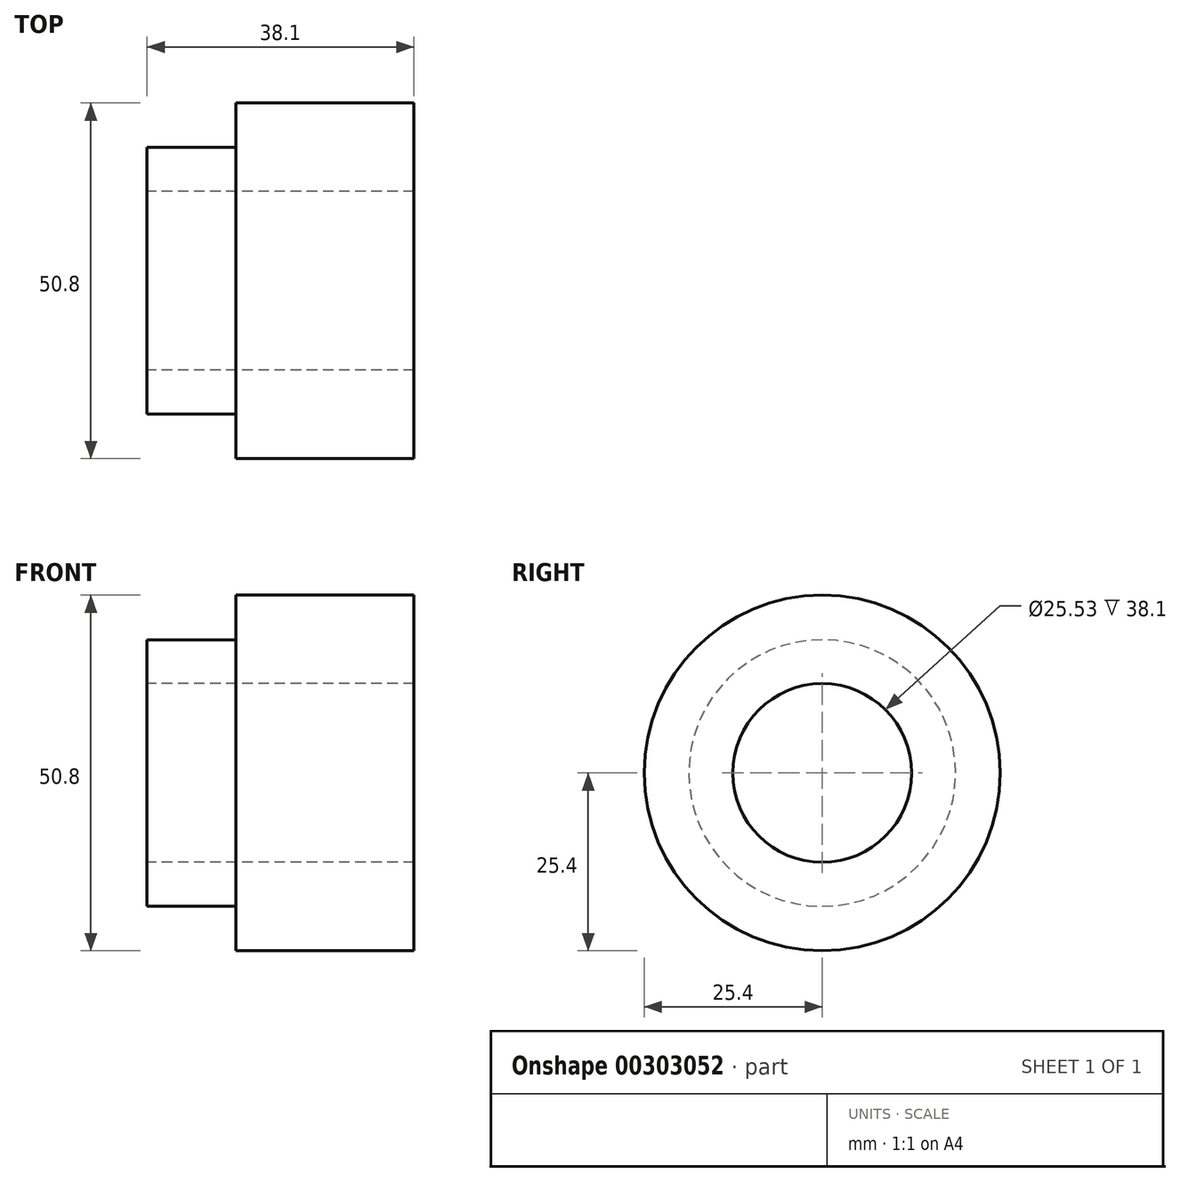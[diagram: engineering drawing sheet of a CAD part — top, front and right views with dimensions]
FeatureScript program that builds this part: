
annotation { "Feature Type Name" : "Feature", "Feature Type Description" : "" }
export const myFeature = defineFeature(function(context is Context, id is Id, definition is map)
    precondition{}
    {
        {
            var Q0;
            Q0=qCreatedBy(makeId("Front.planeOp"),FACE);
            var sketch = newSketch(context, id + "F0", { "sketchPlane" : qUnion([Q0])});
            skLineSegment(sketch, "E0", {"start": v(-19.05, 19.04) * mm, "end": v(-19.05, -19.04) * mm});
            skLineSegment(sketch, "E1", {"start": v(19.05, 25.4) * mm, "end": v(19.05, -25.4) * mm});
            skLineSegment(sketch, "E2", {"start": v(19.05, 25.4) * mm, "end": v(-6.35, 25.4) * mm});
            skLineSegment(sketch, "E3", {"start": v(19.05, -25.4) * mm, "end": v(-6.35, -25.4) * mm});
            skLineSegment(sketch, "E4", {"start": v(-19.05, 19.04) * mm, "end": v(-6.35, 19.04) * mm});
            skLineSegment(sketch, "E5", {"start": v(-6.35, 25.4) * mm, "end": v(-6.35, 19.04) * mm});
            skLineSegment(sketch, "E6", {"start": v(-19.05, -19.04) * mm, "end": v(-6.35, -19.04) * mm});
            skLineSegment(sketch, "E7", {"start": v(-6.35, -19.04) * mm, "end": v(-6.35, -25.4) * mm});
            skLineSegment(sketch, "E8", {"start": v(-19.05, 12.76) * mm, "end": v(19.05, 12.76) * mm});
            skLineSegment(sketch, "E9", {"start": v(-19.05, -12.76) * mm, "end": v(19.05, -12.76) * mm});
            skLineSegment(sketch, "E10", {"start": v(-35.87, 0) * mm, "end": v(41.92, 0) * mm, "construction": true});
            skSolve(sketch);
        }
        {
            var Q0;
            {var subQ1=sQuery(id+"F0.wireOp",EDGE,"E2");Q0=makeQuery(id+"F0.imprint","IMPRINT",FACE,{"disambiguationData":[TD([[makeQuery(id+"F0.imprint","IMPRINT",EDGE,{"derivedFrom":subQ1}),1.0]])]});}
            var Q1;
            Q1=sQuery(id+"F0.wireOp",EDGE,"E10");
            revolve(context, id + "F1", {"entities" : qUnion([Q0]), "axis" : qUnion([Q1]), "revolveType" : RevolveType.FULL});
        }
    });
